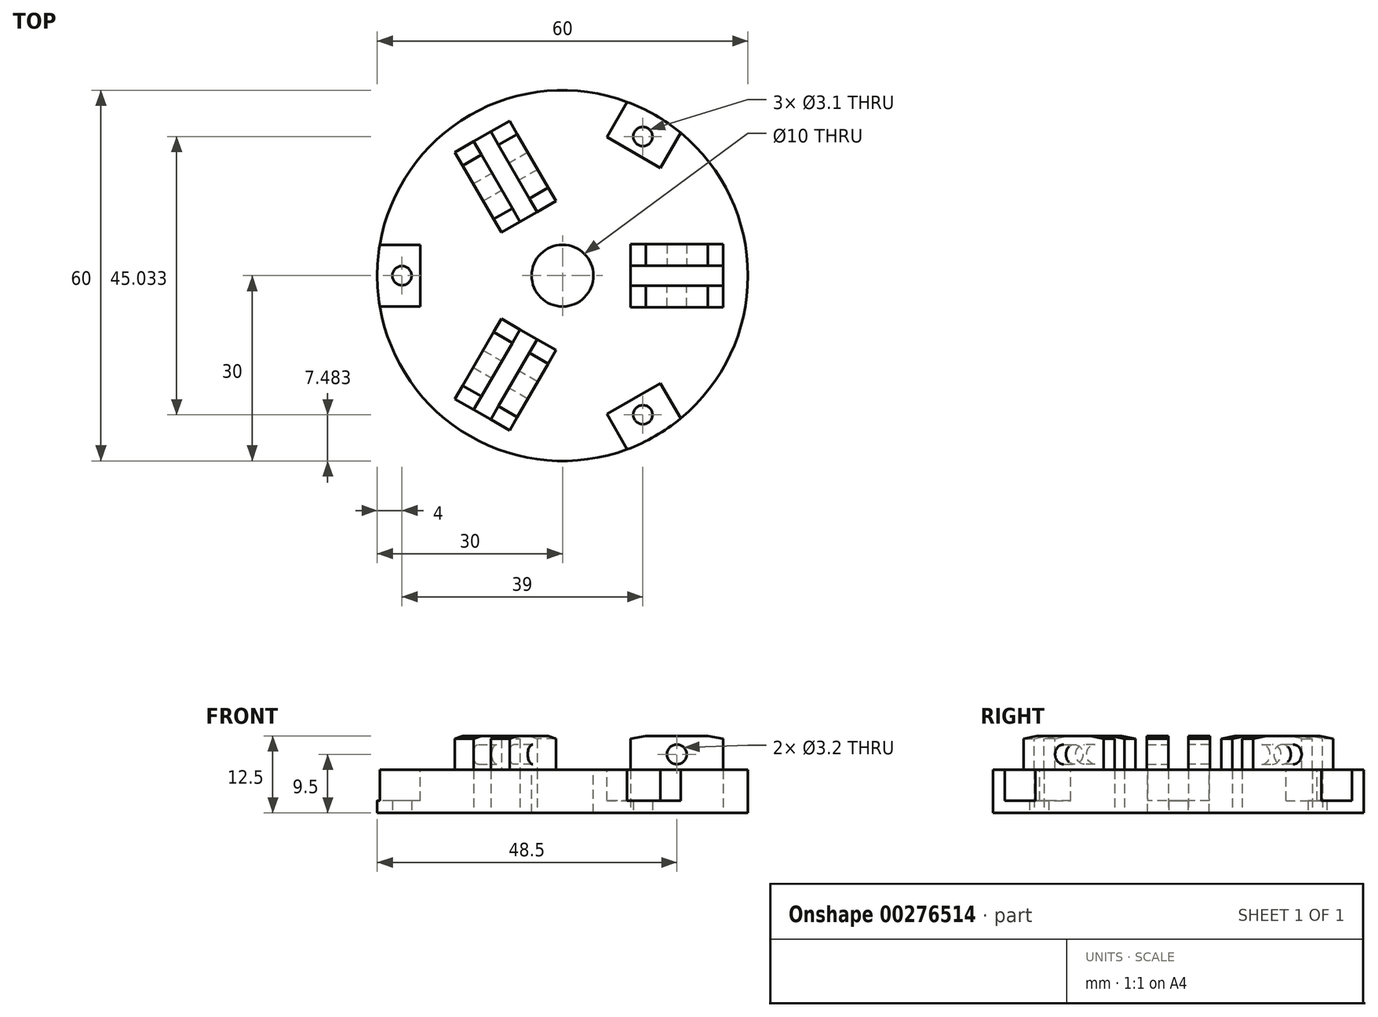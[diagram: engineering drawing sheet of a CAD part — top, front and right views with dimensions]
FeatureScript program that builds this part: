
annotation { "Feature Type Name" : "Feature", "Feature Type Description" : "" }
export const myFeature = defineFeature(function(context is Context, id is Id, definition is map)
    precondition{}
    {
        {
            var Q0;
            Q0=qCreatedBy(makeId("Top.planeOp"),FACE);
            var sketch = newSketch(context, id + "F0", { "sketchPlane" : qUnion([Q0])});
            skLineSegment(sketch, "E0.bottom", {"start": v(26, -1.6) * mm, "end": v(11, -1.6) * mm});
            skLineSegment(sketch, "E0.top", {"start": v(26, 1.6) * mm, "end": v(11, 1.6) * mm});
            skLineSegment(sketch, "E0.left", {"start": v(26, -1.6) * mm, "end": v(26, 1.6) * mm});
            skLineSegment(sketch, "E0.right", {"start": v(11, -1.6) * mm, "end": v(11, 1.6) * mm});
            skPoint(sketch, "E0.middle", {"position": v(18.5, 0) * mm});
            skPoint(sketch, "E1.1.0", {"position": v(-9.25, 16.02) * mm});
            skLineSegment(sketch, "E1.1.1", {"start": v(-14.39, 21.72) * mm, "end": v(-6.89, 8.73) * mm});
            skLineSegment(sketch, "E1.1.2", {"start": v(-4.11, 10.33) * mm, "end": v(-6.89, 8.73) * mm});
            skLineSegment(sketch, "E1.1.3", {"start": v(-11.61, 23.32) * mm, "end": v(-4.11, 10.33) * mm});
            skLineSegment(sketch, "E1.1.4", {"start": v(-11.61, 23.32) * mm, "end": v(-14.39, 21.72) * mm});
            skPoint(sketch, "E1.2.0", {"position": v(-9.25, -16.02) * mm});
            skLineSegment(sketch, "E1.2.1", {"start": v(-11.61, -23.32) * mm, "end": v(-4.11, -10.33) * mm});
            skLineSegment(sketch, "E1.2.2", {"start": v(-6.89, -8.73) * mm, "end": v(-4.11, -10.33) * mm});
            skLineSegment(sketch, "E1.2.3", {"start": v(-14.39, -21.72) * mm, "end": v(-6.89, -8.73) * mm});
            skLineSegment(sketch, "E1.2.4", {"start": v(-14.39, -21.72) * mm, "end": v(-11.61, -23.32) * mm});
            skPoint(sketch, "E1.center", {"position": v(0, 0) * mm});
            skCircle(sketch, "E2", {"center": v(0, 0) * mm, "radius": 30 * mm});
            skLineSegment(sketch, "E3", {"start": v(-30, 0) * mm, "end": v(-26, 0) * mm, "construction": true});
            skCircle(sketch, "E4", {"center": v(-26, 0) * mm, "radius": 1.55 * mm});
            skCircle(sketch, "E5.1.0", {"center": v(13, -22.52) * mm, "radius": 1.55 * mm});
            skCircle(sketch, "E5.2.0", {"center": v(13, 22.52) * mm, "radius": 1.55 * mm});
            skSolve(sketch);
        }
        {
            var Q0;
            Q0=makeQuery(id+"F0.imprint","IMPRINT",FACE,{"disambiguationData":[TD([[makeQuery(id+"F0.imprint","IMPRINT",EDGE,{"derivedFrom":sQuery(id+"F0.wireOp",EDGE,"E0.bottom")}),1.0]])]});
            extrude(context, id + "F1", {"entities" : qUnion([Q0]), "depth" : 7 * mm});
        }
        {
            var Q0;
            Q0=qCreatedBy(makeId("Front.planeOp"),FACE);
            cPlane(context, id + "F2", {"entities" : qUnion([Q0]), "cplaneType" : CPlaneType.OFFSET, "offset" : 1.6 * mm, "width" : 150 * mm, "height" : 150 * mm});
        }
        {
            var Q0;
            Q0=qCreatedBy(id+"F2.planeOp",FACE);
            var sketch = newSketch(context, id + "F3", { "sketchPlane" : qUnion([Q0])});
            skLineSegment(sketch, "E6.0", {"start": v(26, 7) * mm, "end": v(11, 7) * mm});
            skLineSegment(sketch, "E7", {"start": v(26, 7) * mm, "end": v(26, 12) * mm});
            skLineSegment(sketch, "E8", {"start": v(11, 12) * mm, "end": v(11, 7) * mm});
            skLineSegment(sketch, "E9", {"start": v(26, 9.5) * mm, "end": v(18.5, 9.5) * mm, "construction": true});
            skPoint(sketch, "E9.endSnap0", {"position": v(18.5, 7) * mm});
            skCircle(sketch, "E10", {"center": v(18.5, 9.5) * mm, "radius": 1.6 * mm});
            skLineSegment(sketch, "E11", {"start": v(26, 12) * mm, "end": v(23.5, 12.5) * mm});
            skLineSegment(sketch, "E12", {"start": v(23.5, 12.5) * mm, "end": v(13.5, 12.5) * mm});
            skLineSegment(sketch, "E13", {"start": v(13.5, 12.5) * mm, "end": v(11, 12) * mm});
            skSolve(sketch);
        }
        {
            var Q0;
            Q0=makeQuery(id+"F3.imprint","IMPRINT",FACE,{"disambiguationData":[TD([[makeQuery(id+"F3.imprint","IMPRINT",EDGE,{"derivedFrom":sQuery(id+"F3.wireOp",EDGE,"E6.0")}),-1.0]])]});
            extrude(context, id + "F4", {"entities" : qUnion([Q0]), "depth" : 3.5 * mm});
        }
        {
            var Q0;
            Q0=makeQuery(id+"F4.opExtrude","SWEPT_BODY",BODY,{"disambiguationData":[OSD([sQuery(id+"F3.wireOp",EDGE,"E6.0"),sQuery(id+"F3.wireOp",EDGE,"E7"),sQuery(id+"F3.wireOp",EDGE,"E8"),sQuery(id+"F3.wireOp",EDGE,"E10"),sQuery(id+"F3.wireOp",EDGE,"E11"),sQuery(id+"F3.wireOp",EDGE,"E12"),sQuery(id+"F3.wireOp",EDGE,"E13")])]});
            var Q1;
            Q1=qCreatedBy(makeId("Front.planeOp"),FACE);
            mirror(context, id + "F5", {"entities" : qUnion([Q0]), "mirrorPlane" : qUnion([Q1])});
        }
        {
            var Q0;
            Q0=qCreatedBy(makeId("Front.planeOp"),FACE);
            var sketch = newSketch(context, id + "F6", { "sketchPlane" : qUnion([Q0])});
            skLineSegment(sketch, "E14", {"start": v(0, 0) * mm, "end": v(0, 34.97) * mm, "construction": true});
            skSolve(sketch);
        }
        {
            var Q0;
            Q0=makeQuery(id+"F5.opPattern","COPY",BODY,{"derivedFrom":makeQuery(id+"F4.opExtrude","SWEPT_BODY",BODY,{"disambiguationData":[OSD([sQuery(id+"F3.wireOp",EDGE,"E6.0"),sQuery(id+"F3.wireOp",EDGE,"E7"),sQuery(id+"F3.wireOp",EDGE,"E8"),sQuery(id+"F3.wireOp",EDGE,"E10"),sQuery(id+"F3.wireOp",EDGE,"E11"),sQuery(id+"F3.wireOp",EDGE,"E12"),sQuery(id+"F3.wireOp",EDGE,"E13")])]}),"instanceName":"1"});
            var Q1;
            Q1=makeQuery(id+"F4.opExtrude","SWEPT_BODY",BODY,{"disambiguationData":[OSD([sQuery(id+"F3.wireOp",EDGE,"E6.0"),sQuery(id+"F3.wireOp",EDGE,"E7"),sQuery(id+"F3.wireOp",EDGE,"E8"),sQuery(id+"F3.wireOp",EDGE,"E10"),sQuery(id+"F3.wireOp",EDGE,"E11"),sQuery(id+"F3.wireOp",EDGE,"E12"),sQuery(id+"F3.wireOp",EDGE,"E13")])]});
            var Q2;
            Q2=sQuery(id+"F6.wireOp",EDGE,"E14");
            circularPattern(context, id + "F7", {"operationType" : NewBodyOperationType.ADD, "entities" : qUnion([Q0, Q1]), "axis" : qUnion([Q2]), "angle" : 360 * degree, "instanceCount" : 3, "equalSpace" : true});
        }
        {
            var Q0;
            Q0=makeQuery(id+"F1.opExtrude","CAP_FACE",FACE,{"disambiguationData":[OSD([sQuery(id+"F0.wireOp",EDGE,"E0.bottom"),sQuery(id+"F0.wireOp",EDGE,"E0.top"),sQuery(id+"F0.wireOp",EDGE,"E0.left"),sQuery(id+"F0.wireOp",EDGE,"E0.right"),sQuery(id+"F0.wireOp",EDGE,"E1.1.1"),sQuery(id+"F0.wireOp",EDGE,"E1.1.2"),sQuery(id+"F0.wireOp",EDGE,"E1.1.3"),sQuery(id+"F0.wireOp",EDGE,"E1.1.4"),sQuery(id+"F0.wireOp",EDGE,"E1.2.1"),sQuery(id+"F0.wireOp",EDGE,"E1.2.2"),sQuery(id+"F0.wireOp",EDGE,"E1.2.3"),sQuery(id+"F0.wireOp",EDGE,"E1.2.4"),sQuery(id+"F0.wireOp",EDGE,"E2"),sQuery(id+"F0.wireOp",EDGE,"E4"),sQuery(id+"F0.wireOp",EDGE,"E5.1.0"),sQuery(id+"F0.wireOp",EDGE,"E5.2.0")])],"isStart":false});
            var sketch = newSketch(context, id + "F8", { "sketchPlane" : qUnion([Q0])});
            skCircle(sketch, "E15", {"center": v(0, 0) * mm, "radius": 5 * mm});
            skSolve(sketch);
        }
        {
            var Q0;
            Q0=makeQuery(id+"F8.imprint","IMPRINT",FACE,{"disambiguationData":[TD([[makeQuery(id+"F8.imprint","IMPRINT",EDGE,{"derivedFrom":sQuery(id+"F8.wireOp",EDGE,"E15")}),1.0]])]});
            extrude(context, id + "F9", {"entities" : qUnion([Q0]), "operationType" : NewBodyOperationType.REMOVE, "oppositeDirection" : true, "depth" : 25 * mm});
        }
        {
            var Q0;
            Q0=makeQuery(id+"F1.opExtrude","CAP_FACE",FACE,{"disambiguationData":[OSD([sQuery(id+"F0.wireOp",EDGE,"E0.bottom"),sQuery(id+"F0.wireOp",EDGE,"E0.top"),sQuery(id+"F0.wireOp",EDGE,"E0.left"),sQuery(id+"F0.wireOp",EDGE,"E0.right"),sQuery(id+"F0.wireOp",EDGE,"E1.1.1"),sQuery(id+"F0.wireOp",EDGE,"E1.1.2"),sQuery(id+"F0.wireOp",EDGE,"E1.1.3"),sQuery(id+"F0.wireOp",EDGE,"E1.1.4"),sQuery(id+"F0.wireOp",EDGE,"E1.2.1"),sQuery(id+"F0.wireOp",EDGE,"E1.2.2"),sQuery(id+"F0.wireOp",EDGE,"E1.2.3"),sQuery(id+"F0.wireOp",EDGE,"E1.2.4"),sQuery(id+"F0.wireOp",EDGE,"E2"),sQuery(id+"F0.wireOp",EDGE,"E4"),sQuery(id+"F0.wireOp",EDGE,"E5.1.0"),sQuery(id+"F0.wireOp",EDGE,"E5.2.0")])],"isStart":false});
            var sketch = newSketch(context, id + "F10", { "sketchPlane" : qUnion([Q0])});
            skLineSegment(sketch, "E16", {"start": v(-26, 0) * mm, "end": v(-30, 0) * mm, "construction": true});
            skLineSegment(sketch, "E17", {"start": v(-30, 0) * mm, "end": v(-30, 5) * mm});
            skLineSegment(sketch, "E18", {"start": v(-23, 5) * mm, "end": v(-23, 0) * mm});
            skLineSegment(sketch, "E19.MirrorCS", {"start": v(-30, 0) * mm, "end": v(-30, -5) * mm});
            skLineSegment(sketch, "E20.MirrorCS", {"start": v(-23, -5) * mm, "end": v(-23, 0) * mm});
            skPoint(sketch, "E21.center", {"position": v(0, 0) * mm});
            skLineSegment(sketch, "E22", {"start": v(-23, 5) * mm, "end": v(-30, 5) * mm});
            skLineSegment(sketch, "E23", {"start": v(-23, -5) * mm, "end": v(-30, -5) * mm});
            skLineSegment(sketch, "E24.1.0", {"start": v(7.17, -22.42) * mm, "end": v(10.67, -28.48) * mm});
            skLineSegment(sketch, "E24.1.1", {"start": v(15.83, -17.42) * mm, "end": v(11.5, -19.92) * mm});
            skLineSegment(sketch, "E24.1.2", {"start": v(15, -25.98) * mm, "end": v(19.33, -23.48) * mm});
            skLineSegment(sketch, "E24.1.3", {"start": v(7.17, -22.42) * mm, "end": v(11.5, -19.92) * mm});
            skLineSegment(sketch, "E24.1.4", {"start": v(15, -25.98) * mm, "end": v(10.67, -28.48) * mm});
            skLineSegment(sketch, "E24.1.5", {"start": v(13, -22.52) * mm, "end": v(15, -25.98) * mm, "construction": true});
            skLineSegment(sketch, "E24.1.6", {"start": v(15.83, -17.42) * mm, "end": v(19.33, -23.48) * mm});
            skLineSegment(sketch, "E24.2.0", {"start": v(15.83, 17.42) * mm, "end": v(19.33, 23.48) * mm});
            skLineSegment(sketch, "E24.2.1", {"start": v(7.17, 22.42) * mm, "end": v(11.5, 19.92) * mm});
            skLineSegment(sketch, "E24.2.2", {"start": v(15, 25.98) * mm, "end": v(10.67, 28.48) * mm});
            skLineSegment(sketch, "E24.2.3", {"start": v(15.83, 17.42) * mm, "end": v(11.5, 19.92) * mm});
            skLineSegment(sketch, "E24.2.4", {"start": v(15, 25.98) * mm, "end": v(19.33, 23.48) * mm});
            skLineSegment(sketch, "E24.2.5", {"start": v(13, 22.52) * mm, "end": v(15, 25.98) * mm, "construction": true});
            skLineSegment(sketch, "E24.2.6", {"start": v(7.17, 22.42) * mm, "end": v(10.67, 28.48) * mm});
            skSolve(sketch);
        }
        {
            var Q0;
            Q0 = qSketchRegion(id + "F10", true);
            extrude(context, id + "F11", {"entities" : qUnion([Q0]), "operationType" : NewBodyOperationType.REMOVE, "oppositeDirection" : true, "depth" : 5 * mm});
        }
    });
